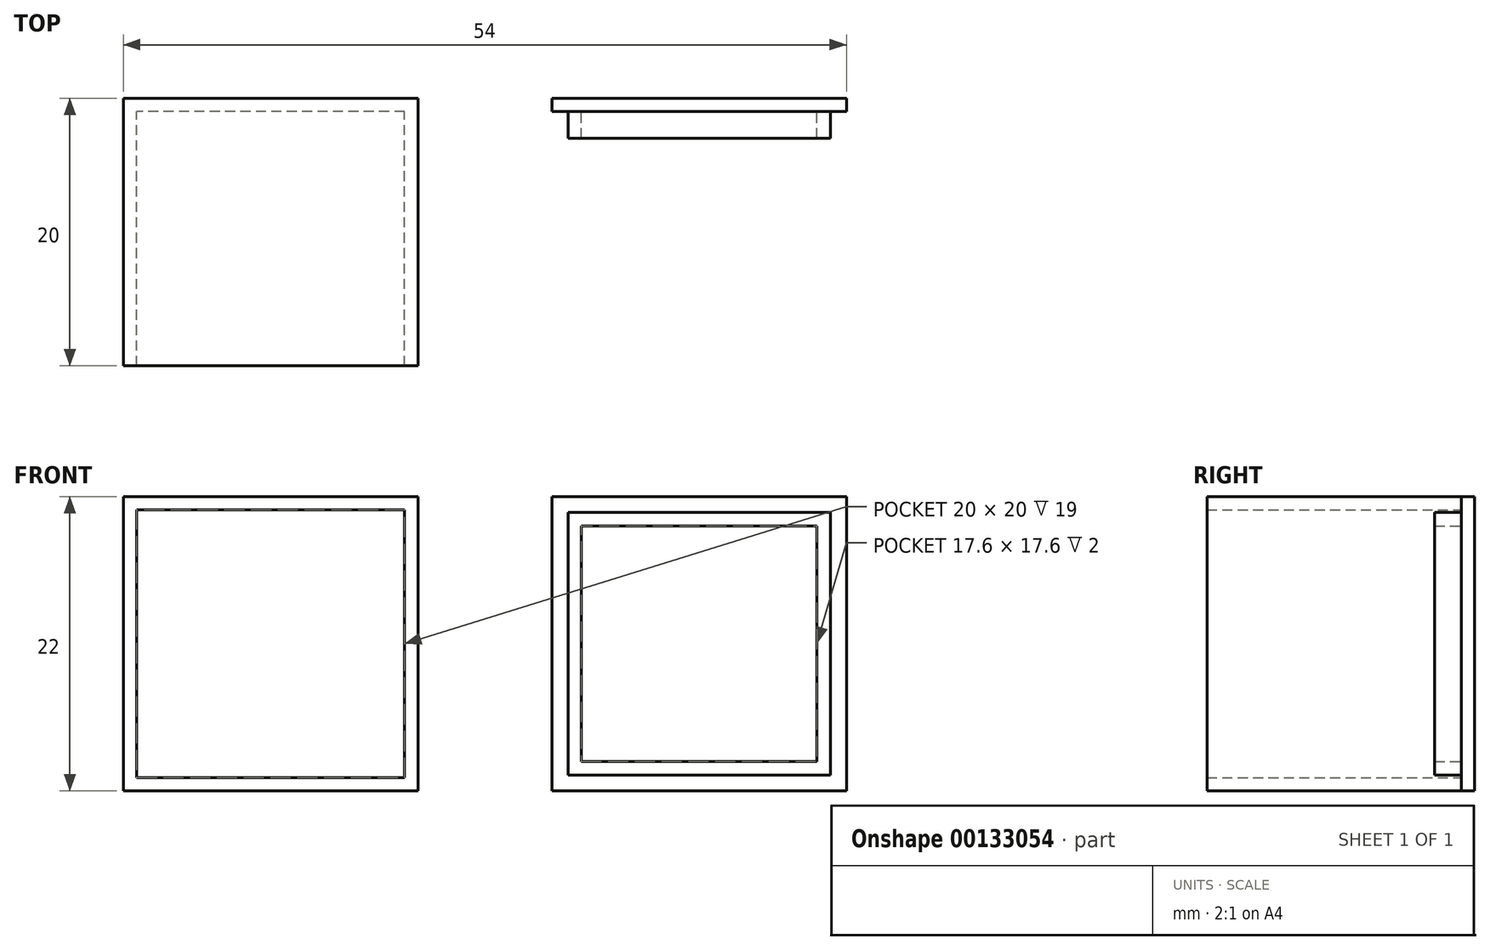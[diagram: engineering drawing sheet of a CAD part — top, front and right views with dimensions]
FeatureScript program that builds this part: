
annotation { "Feature Type Name" : "Feature", "Feature Type Description" : "" }
export const myFeature = defineFeature(function(context is Context, id is Id, definition is map)
    precondition{}
    {
        {
            var Q0;
            Q0=qCreatedBy(makeId("Front.planeOp"),FACE);
            var sketch = newSketch(context, id + "F0", { "sketchPlane" : qUnion([Q0])});
            skLineSegment(sketch, "E0.bottom", {"start": v(0, 0) * mm, "end": v(22, 0) * mm});
            skLineSegment(sketch, "E0.top", {"start": v(0, 22) * mm, "end": v(22, 22) * mm});
            skLineSegment(sketch, "E0.left", {"start": v(0, 0) * mm, "end": v(0, 22) * mm});
            skLineSegment(sketch, "E0.right", {"start": v(22, 0) * mm, "end": v(22, 22) * mm});
            skLineSegment(sketch, "E1.bottom", {"start": v(1, 21) * mm, "end": v(21, 21) * mm});
            skLineSegment(sketch, "E1.top", {"start": v(1, 1) * mm, "end": v(21, 1) * mm});
            skLineSegment(sketch, "E1.left", {"start": v(1, 21) * mm, "end": v(1, 1) * mm});
            skLineSegment(sketch, "E1.right", {"start": v(21, 21) * mm, "end": v(21, 1) * mm});
            skLineSegment(sketch, "E2", {"start": v(11, 0) * mm, "end": v(11, 22) * mm, "construction": true});
            skLineSegment(sketch, "E3", {"start": v(0, 11) * mm, "end": v(22, 11) * mm, "construction": true});
            skLineSegment(sketch, "E4", {"start": v(32, 11) * mm, "end": v(54, 11) * mm, "construction": true});
            skLineSegment(sketch, "E5", {"start": v(43, 0) * mm, "end": v(43, 22) * mm, "construction": true});
            skLineSegment(sketch, "E6.bottom", {"start": v(32, 22) * mm, "end": v(54, 22) * mm});
            skLineSegment(sketch, "E6.top", {"start": v(32, 0) * mm, "end": v(54, 0) * mm});
            skLineSegment(sketch, "E6.left", {"start": v(32, 22) * mm, "end": v(32, 0) * mm});
            skLineSegment(sketch, "E6.right", {"start": v(54, 22) * mm, "end": v(54, 0) * mm});
            skLineSegment(sketch, "E7.bottom", {"start": v(33, 21) * mm, "end": v(53, 21) * mm, "construction": true});
            skLineSegment(sketch, "E7.top", {"start": v(33, 1) * mm, "end": v(53, 1) * mm, "construction": true});
            skLineSegment(sketch, "E7.left", {"start": v(33, 21) * mm, "end": v(33, 1) * mm, "construction": true});
            skLineSegment(sketch, "E7.right", {"start": v(53, 21) * mm, "end": v(53, 1) * mm, "construction": true});
            skLineSegment(sketch, "E8.bottom", {"start": v(33.2, 20.8) * mm, "end": v(52.8, 20.8) * mm});
            skLineSegment(sketch, "E8.top", {"start": v(33.2, 1.2) * mm, "end": v(52.8, 1.2) * mm});
            skLineSegment(sketch, "E8.left", {"start": v(33.2, 20.8) * mm, "end": v(33.2, 1.2) * mm});
            skLineSegment(sketch, "E8.right", {"start": v(52.8, 20.8) * mm, "end": v(52.8, 1.2) * mm});
            skLineSegment(sketch, "E9", {"start": v(1, 21) * mm, "end": v(0, 21) * mm, "construction": true});
            skLineSegment(sketch, "E10", {"start": v(1, 21) * mm, "end": v(1, 22) * mm, "construction": true});
            skText(sketch, "E11", { "text": "Длина\nШирина\nТолщина стенок\nЗазор в ответной части", "fontName": "OpenSans-Regular.ttf"});
            skLineSegment(sketch, "E12", {"start": v(12.68, 42) * mm, "end": v(32.68, 42) * mm, "construction": true});
            skLineSegment(sketch, "E13", {"start": v(12.68, 39.5) * mm, "end": v(32.68, 39.5) * mm, "construction": true});
            skLineSegment(sketch, "E14", {"start": v(12.68, 37) * mm, "end": v(13.68, 37) * mm, "construction": true});
            skLineSegment(sketch, "E15", {"start": v(12.68, 34.5) * mm, "end": v(12.88, 34.5) * mm, "construction": true});
            skLineSegment(sketch, "E16", {"start": v(33, 21) * mm, "end": v(33, 22) * mm, "construction": true});
            skLineSegment(sketch, "E17", {"start": v(33, 21) * mm, "end": v(32, 21) * mm, "construction": true});
            skLineSegment(sketch, "E18", {"start": v(33.2, 20.8) * mm, "end": v(33.2, 21) * mm, "construction": true});
            skLineSegment(sketch, "E19", {"start": v(33.2, 20.8) * mm, "end": v(33, 20.8) * mm, "construction": true});
            skLineSegment(sketch, "E20.bottom", {"start": v(34.2, 19.8) * mm, "end": v(51.8, 19.8) * mm});
            skLineSegment(sketch, "E20.top", {"start": v(34.2, 2.2) * mm, "end": v(51.8, 2.2) * mm});
            skLineSegment(sketch, "E20.left", {"start": v(34.2, 19.8) * mm, "end": v(34.2, 2.2) * mm});
            skLineSegment(sketch, "E20.right", {"start": v(51.8, 19.8) * mm, "end": v(51.8, 2.2) * mm});
            skLineSegment(sketch, "E21", {"start": v(34.2, 19.8) * mm, "end": v(34.2, 20.8) * mm, "construction": true});
            skLineSegment(sketch, "E22", {"start": v(34.2, 19.8) * mm, "end": v(33.2, 19.8) * mm, "construction": true});
            const initialGuessF0  = {"E11": [-0.0124, 0.04074, 1, 0, 0.00126]};
            skSetInitialGuess(sketch, initialGuessF0);
            skSolve(sketch);
        }
        {
            var Q0;
            Q0=makeQuery(id+"F0.imprint","IMPRINT",FACE,{"disambiguationData":[TD([[makeQuery(id+"F0.imprint","IMPRINT",EDGE,{"derivedFrom":sQuery(id+"F0.wireOp",EDGE,"E1.bottom")}),-1.0]])]});
            var Q1;
            Q1=makeQuery(id+"F0.imprint","IMPRINT",FACE,{"disambiguationData":[TD([[makeQuery(id+"F0.imprint","IMPRINT",EDGE,{"derivedFrom":sQuery(id+"F0.wireOp",EDGE,"E0.bottom")}),1.0]])]});
            var Q2;
            Q2=makeQuery(id+"F0.imprint","IMPRINT",FACE,{"disambiguationData":[TD([[makeQuery(id+"F0.imprint","IMPRINT",EDGE,{"derivedFrom":sQuery(id+"F0.wireOp",EDGE,"E6.bottom")}),-1.0]])]});
            var Q3;
            Q3=makeQuery(id+"F0.imprint","IMPRINT",FACE,{"disambiguationData":[TD([[makeQuery(id+"F0.imprint","IMPRINT",EDGE,{"derivedFrom":sQuery(id+"F0.wireOp",EDGE,"E7.bottom")}),-1.0]])]});
            var Q4;
            Q4=makeQuery(id+"F0.imprint","IMPRINT",FACE,{"disambiguationData":[TD([[makeQuery(id+"F0.imprint","IMPRINT",EDGE,{"derivedFrom":sQuery(id+"F0.wireOp",EDGE,"E8.bottom")}),-1.0]])]});
            var Q5;
            Q5=makeQuery(id+"F0.imprint","IMPRINT",FACE,{"disambiguationData":[TD([[makeQuery(id+"F0.imprint","IMPRINT",EDGE,{"derivedFrom":sQuery(id+"F0.wireOp",EDGE,"E20.bottom")}),-1.0]])]});
            extrude(context, id + "F1", {"entities" : qUnion([Q0, Q1, Q2, Q3, Q4, Q5]), "depth" : 1 * mm});
        }
        {
            var Q0;
            Q0=makeQuery(id+"F0.imprint","IMPRINT",FACE,{"disambiguationData":[TD([[makeQuery(id+"F0.imprint","IMPRINT",EDGE,{"derivedFrom":sQuery(id+"F0.wireOp",EDGE,"E0.bottom")}),1.0]])]});
            extrude(context, id + "F2", {"entities" : qUnion([Q0]), "operationType" : NewBodyOperationType.ADD, "depth" : 20 * mm});
        }
        {
            var Q0;
            Q0=makeQuery(id+"F0.imprint","IMPRINT",FACE,{"disambiguationData":[TD([[makeQuery(id+"F0.imprint","IMPRINT",EDGE,{"derivedFrom":sQuery(id+"F0.wireOp",EDGE,"E8.bottom")}),-1.0]])]});
            extrude(context, id + "F3", {"entities" : qUnion([Q0]), "operationType" : NewBodyOperationType.ADD, "depth" : (1 + 2) * mm});
        }
    });
